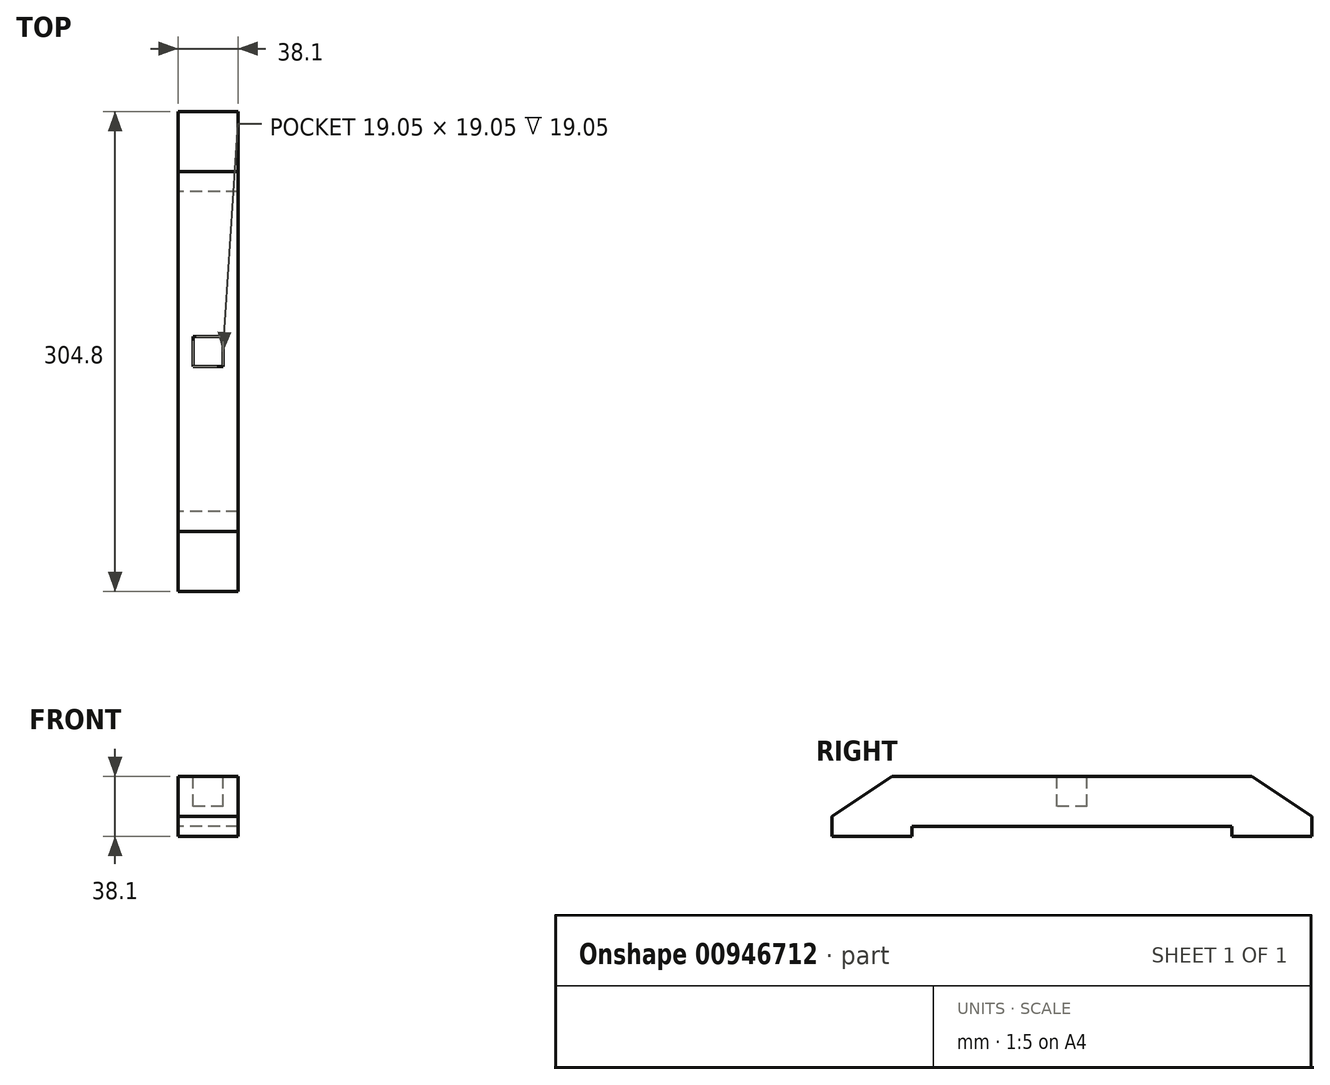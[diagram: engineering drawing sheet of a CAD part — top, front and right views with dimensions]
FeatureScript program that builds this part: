
annotation { "Feature Type Name" : "Feature", "Feature Type Description" : "" }
export const myFeature = defineFeature(function(context is Context, id is Id, definition is map)
    precondition{}
    {
        {
            var Q0;
            Q0=qCreatedBy(makeId("Right.planeOp"),FACE);
            var sketch = newSketch(context, id + "F0", { "sketchPlane" : qUnion([Q0])});
            skLineSegment(sketch, "E0.bottom", {"start": v(114.3, 19.05) * mm, "end": v(-114.3, 19.05) * mm});
            skLineSegment(sketch, "E0.top", {"start": v(152.4, -19.05) * mm, "end": v(101.6, -19.05) * mm});
            skLineSegment(sketch, "E0.left", {"start": v(152.4, -6.35) * mm, "end": v(152.4, -19.05) * mm});
            skLineSegment(sketch, "E0.right", {"start": v(-152.4, -6.35) * mm, "end": v(-152.4, -19.05) * mm});
            skPoint(sketch, "E0.middle", {"position": v(0, 0) * mm});
            skLineSegment(sketch, "E1", {"start": v(152.4, -19.05) * mm, "end": v(152.4, -6.35) * mm});
            skLineSegment(sketch, "E2", {"start": v(152.4, -6.35) * mm, "end": v(114.3, 19.05) * mm});
            skLineSegment(sketch, "E3.MirrorCS", {"start": v(-152.4, -6.35) * mm, "end": v(-114.3, 19.05) * mm});
            skLineSegment(sketch, "E4.bottom", {"start": v(101.6, -12.7) * mm, "end": v(-101.6, -12.7) * mm});
            skLineSegment(sketch, "E4.left", {"start": v(101.6, -12.7) * mm, "end": v(101.6, -25.4) * mm});
            skLineSegment(sketch, "E4.right", {"start": v(-101.6, -12.7) * mm, "end": v(-101.6, -19.05) * mm});
            skPoint(sketch, "E4.middle", {"position": v(0, -19.05) * mm});
            skPoint(sketch, "E5.orphan", {"position": v(-152.4, 19.05) * mm});
            skPoint(sketch, "E6.orphan", {"position": v(-101.6, -25.4) * mm});
            skLineSegment(sketch, "E7.trimOffspring", {"start": v(-101.6, -19.05) * mm, "end": v(-152.4, -19.05) * mm});
            skPoint(sketch, "E8.orphan", {"position": v(152.4, 19.05) * mm});
            skSolve(sketch);
        }
        {
            var Q0;
            Q0 = qSketchRegion(id + "F0", true);
            extrude(context, id + "F1", {"entities" : qUnion([Q0]), "depth" : 38.1 * mm, "offsetDistance" : 25.4 * mm});
        }
        {
            var Q0;
            Q0=makeQuery(id+"F1.opExtrude","SWEPT_FACE",FACE,{"disambiguationData":[OSD([sQuery(id+"F0.wireOp",EDGE,"E0.bottom")])]});
            var sketch = newSketch(context, id + "F2", { "sketchPlane" : qUnion([Q0])});
            skLineSegment(sketch, "E9", {"start": v(0, 0) * mm, "end": v(38.1, 0) * mm});
            skLineSegment(sketch, "E10.bottom", {"start": v(28.58, 9.53) * mm, "end": v(9.52, 9.53) * mm});
            skLineSegment(sketch, "E10.top", {"start": v(28.58, -9.52) * mm, "end": v(9.53, -9.52) * mm});
            skLineSegment(sketch, "E10.left", {"start": v(28.58, 9.53) * mm, "end": v(28.58, -9.52) * mm});
            skLineSegment(sketch, "E10.right", {"start": v(9.52, 9.53) * mm, "end": v(9.52, -9.52) * mm});
            skPoint(sketch, "E10.middle", {"position": v(19.05, 0) * mm});
            skSolve(sketch);
        }
        {
            var Q0;
            Q0 = qSketchRegion(id + "F2", true);
            extrude(context, id + "F3", {"entities" : qUnion([Q0]), "operationType" : NewBodyOperationType.REMOVE, "oppositeDirection" : true, "depth" : 19.05 * mm, "offsetDistance" : 25.4 * mm});
        }
        {
            var Q0;
            Q0=makeQuery(id+"F1.opExtrude","SWEPT_BODY",BODY,{"disambiguationData":[OSD([sQuery(id+"F0.wireOp",EDGE,"E0.bottom"),sQuery(id+"F0.wireOp",EDGE,"E0.top"),sQuery(id+"F0.wireOp",EDGE,"E0.right"),sQuery(id+"F0.wireOp",EDGE,"E1"),sQuery(id+"F0.wireOp",EDGE,"E2"),sQuery(id+"F0.wireOp",EDGE,"E3.MirrorCS"),sQuery(id+"F0.wireOp",EDGE,"E4.bottom"),sQuery(id+"F0.wireOp",EDGE,"E4.left"),sQuery(id+"F0.wireOp",EDGE,"E4.right"),sQuery(id+"F0.wireOp",EDGE,"E7.trimOffspring")])]});
            transform(context, id + "F4", {"entities" : qUnion([Q0]), "transformType" : TransformType.TRANSLATION_3D, "dx" : 0 * mm, "dy" : 0 * mm, "dz" : 0 * mm, "makeCopy" : true});
        }
        {
            var Q0;
            Q0=makeQuery(id+"F4.opPattern","COPY",BODY,{"derivedFrom":makeQuery(id+"F1.opExtrude","SWEPT_BODY",BODY,{"disambiguationData":[OSD([sQuery(id+"F0.wireOp",EDGE,"E0.bottom"),sQuery(id+"F0.wireOp",EDGE,"E0.top"),sQuery(id+"F0.wireOp",EDGE,"E0.right"),sQuery(id+"F0.wireOp",EDGE,"E1"),sQuery(id+"F0.wireOp",EDGE,"E2"),sQuery(id+"F0.wireOp",EDGE,"E3.MirrorCS"),sQuery(id+"F0.wireOp",EDGE,"E4.bottom"),sQuery(id+"F0.wireOp",EDGE,"E4.left"),sQuery(id+"F0.wireOp",EDGE,"E4.right"),sQuery(id+"F0.wireOp",EDGE,"E7.trimOffspring")])]}),"instanceName":"1"});
            deleteBodies(context, id + "F5", {"entities" : qUnion([Q0])});
        }
    });
